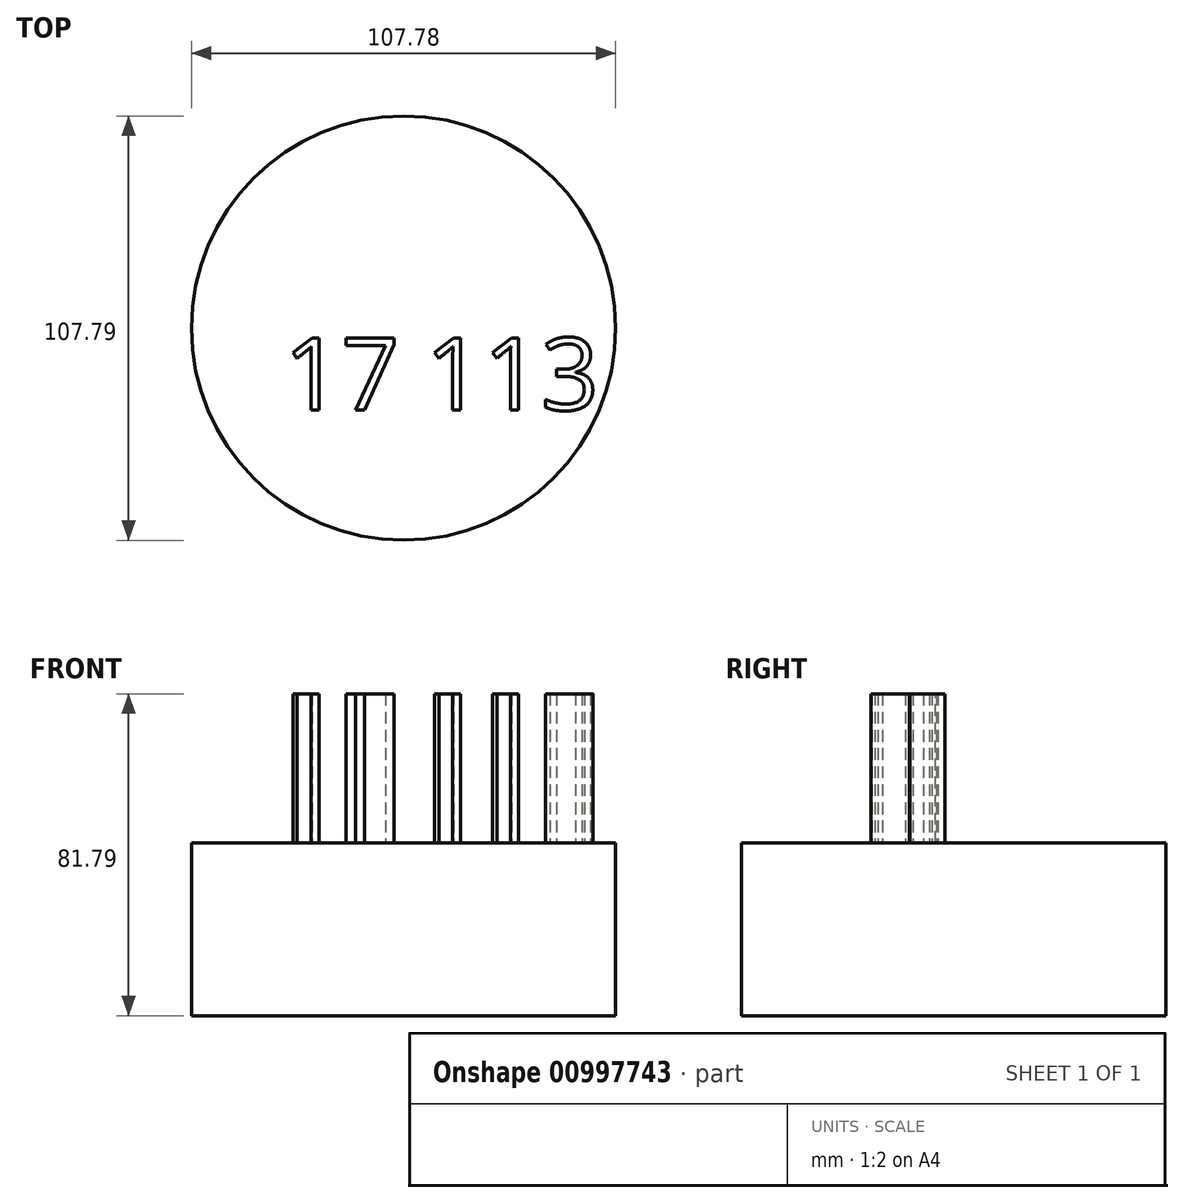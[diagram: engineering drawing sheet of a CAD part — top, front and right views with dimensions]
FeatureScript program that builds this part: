
annotation { "Feature Type Name" : "Feature", "Feature Type Description" : "" }
export const myFeature = defineFeature(function(context is Context, id is Id, definition is map)
    precondition{}
    {
        {
            var Q0;
            Q0=qCreatedBy(makeId("Top.planeOp"),FACE);
            var sketch = newSketch(context, id + "F0", { "sketchPlane" : qUnion([Q0])});
            skCircle(sketch, "E0", {"center": v(0, 2.34) * mm, "radius": 53.9 * mm});
            skSolve(sketch);
        }
        {
            var Q0;
            Q0=makeQuery(id+"F0.imprint","IMPRINT",FACE,{"disambiguationData":[TD([[makeQuery(id+"F0.imprint","IMPRINT",EDGE,{"derivedFrom":sQuery(id+"F0.wireOp",EDGE,"E0")}),1.0]])]});
            extrude(context, id + "F1", {"entities" : qUnion([Q0]), "depth" : 43.94 * mm, "offsetDistance" : 25.4 * mm});
        }
        {
            var Q0;
            Q0=makeQuery(id+"F1.opExtrude","CAP_FACE",FACE,{"disambiguationData":[OSD([sQuery(id+"F0.wireOp",EDGE,"E0")])],"isStart":false});
            var sketch = newSketch(context, id + "F2", { "sketchPlane" : qUnion([Q0])});
            skText(sketch, "E1", { "text": "17 113", "fontName": "OpenSans-Regular.ttf"});
            const initialGuessF2  = {"E1": [-0.03048, -0.01848, 1, 0, 0.01848]};
            skSetInitialGuess(sketch, initialGuessF2);
            skSolve(sketch);
        }
        {
            var Q0;
            Q0 = qSketchRegion(id + "F2", true);
            extrude(context, id + "F3", {"entities" : qUnion([Q0]), "operationType" : NewBodyOperationType.ADD, "depth" : 37.85 * mm, "offsetDistance" : 25.4 * mm});
        }
    });
